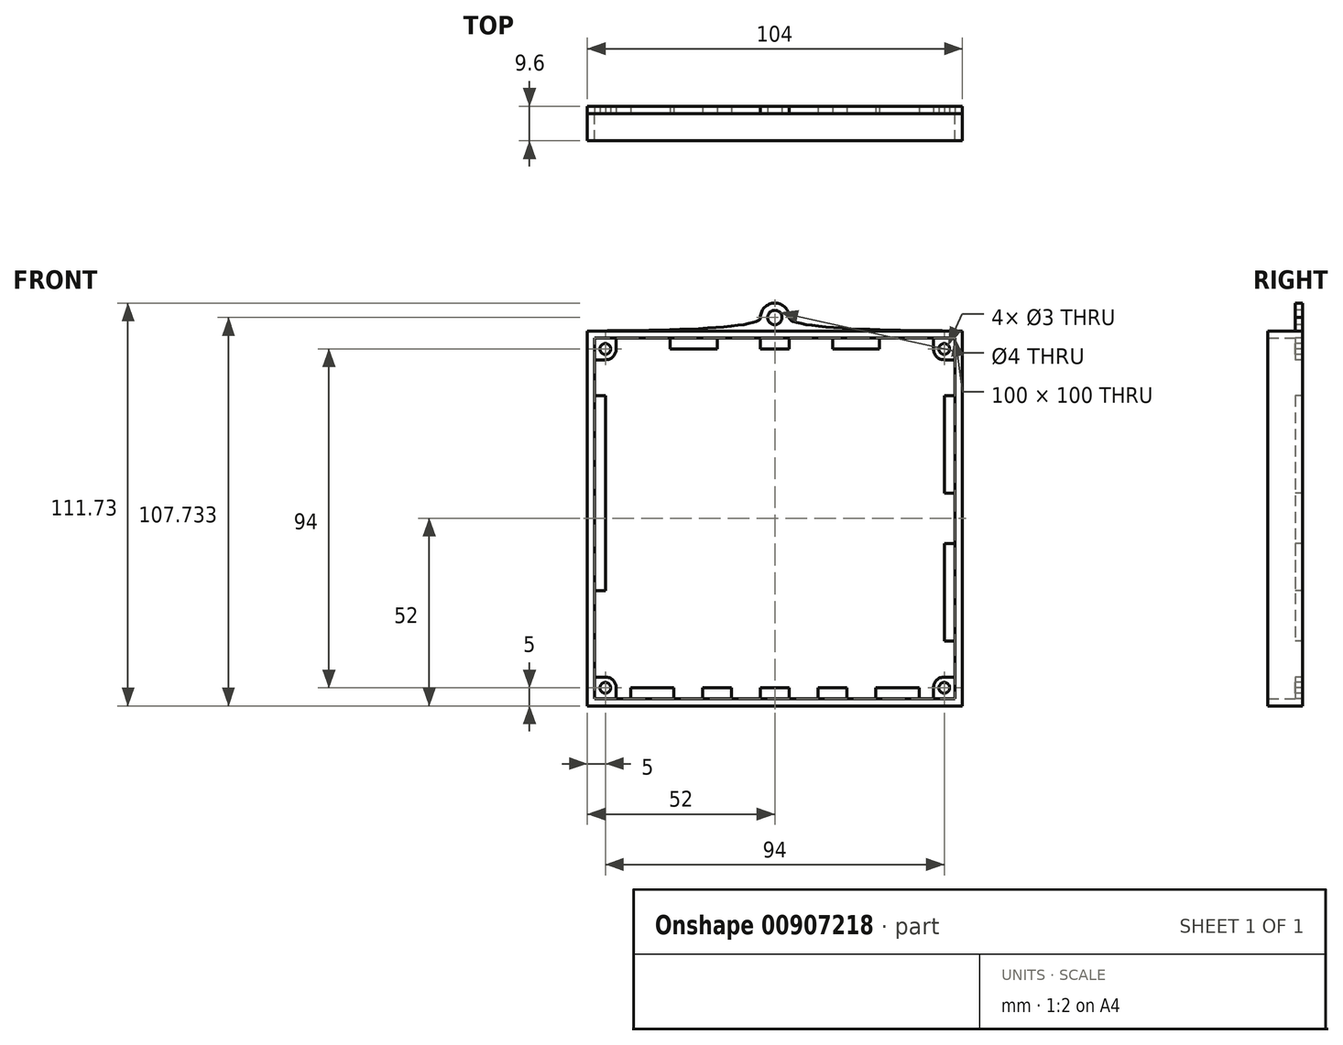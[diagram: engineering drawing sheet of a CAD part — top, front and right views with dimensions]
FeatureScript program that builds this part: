
annotation { "Feature Type Name" : "Feature", "Feature Type Description" : "" }
export const myFeature = defineFeature(function(context is Context, id is Id, definition is map)
    precondition{}
    {
        {
            var Q0;
            Q0=qCreatedBy(makeId("Front.planeOp"),FACE);
            var sketch = newSketch(context, id + "F0", { "sketchPlane" : qUnion([Q0])});
            skLineSegment(sketch, "E0.bottom", {"start": v(50, 50) * mm, "end": v(-50, 50) * mm});
            skLineSegment(sketch, "E0.top", {"start": v(50, -50) * mm, "end": v(-50, -50) * mm});
            skLineSegment(sketch, "E0.left", {"start": v(50, 50) * mm, "end": v(50, -50) * mm});
            skLineSegment(sketch, "E0.right", {"start": v(-50, 50) * mm, "end": v(-50, -50) * mm});
            skPoint(sketch, "E0.middle", {"position": v(0, 0) * mm});
            skLineSegment(sketch, "E1.bottom", {"start": v(-52, 52) * mm, "end": v(52, 52) * mm});
            skLineSegment(sketch, "E1.top", {"start": v(-52, -52) * mm, "end": v(52, -52) * mm});
            skLineSegment(sketch, "E1.left", {"start": v(-52, 52) * mm, "end": v(-52, -52) * mm});
            skLineSegment(sketch, "E1.right", {"start": v(52, 52) * mm, "end": v(52, -52) * mm});
            skSolve(sketch);
        }
        {
            var Q0;
            Q0 = qSketchRegion(id + "F0", true);
            extrude(context, id + "F1", {"entities" : qUnion([Q0]), "depth" : 7.6 * mm, "offsetDistance" : 25 * mm});
        }
        {
            var Q0;
            Q0=qCreatedBy(makeId("Front.planeOp"),FACE);
            var sketch = newSketch(context, id + "F2", { "sketchPlane" : qUnion([Q0])});
            skPoint(sketch, "E2.middle", {"position": v(0, 0) * mm});
            skCircle(sketch, "E3", {"center": v(47, 47) * mm, "radius": 1.5 * mm});
            skLineSegment(sketch, "E4.bottom", {"start": v(47, 47) * mm, "end": v(-47, 47) * mm, "construction": true});
            skLineSegment(sketch, "E4.top", {"start": v(47, -47) * mm, "end": v(-47, -47) * mm, "construction": true});
            skLineSegment(sketch, "E4.left", {"start": v(47, 47) * mm, "end": v(47, -47) * mm, "construction": true});
            skLineSegment(sketch, "E4.right", {"start": v(-47, 47) * mm, "end": v(-47, -47) * mm, "construction": true});
            skLineSegment(sketch, "E5.0", {"start": v(52, 52) * mm, "end": v(52, -52) * mm});
            skLineSegment(sketch, "E6.0", {"start": v(-52, 52) * mm, "end": v(52, 52) * mm, "construction": true});
            skLineSegment(sketch, "E7.0", {"start": v(-52, 52) * mm, "end": v(-52, -52) * mm});
            skLineSegment(sketch, "E8.0", {"start": v(-52, -52) * mm, "end": v(52, -52) * mm});
            skLineSegment(sketch, "E9.0", {"start": v(50, 50) * mm, "end": v(50, -50) * mm, "construction": true});
            skLineSegment(sketch, "E10.0", {"start": v(50, 50) * mm, "end": v(-50, 50) * mm, "construction": true});
            skLineSegment(sketch, "E11.0", {"start": v(-50, 50) * mm, "end": v(-50, -50) * mm, "construction": true});
            skLineSegment(sketch, "E12.0", {"start": v(50, -50) * mm, "end": v(-50, -50) * mm, "construction": true});
            skArc(sketch, "E13", {"start": v(47, 44) * mm, "mid": v(44.88, 44.88) * mm, "end": v(44, 47) * mm});
            skLineSegment(sketch, "E14", {"start": v(47, 44) * mm, "end": v(50, 44) * mm});
            skLineSegment(sketch, "E15", {"start": v(44, 47) * mm, "end": v(44, 50) * mm});
            skArc(sketch, "E16.MirrorCS", {"start": v(-47, 44) * mm, "mid": v(-44.88, 44.88) * mm, "end": v(-44, 47) * mm});
            skCircle(sketch, "E17.MirrorC", {"center": v(-47, 47) * mm, "radius": 1.5 * mm});
            skLineSegment(sketch, "E18.MirrorCS", {"start": v(-44, 47) * mm, "end": v(-44, 50) * mm});
            skLineSegment(sketch, "E19.MirrorCS", {"start": v(-47, 44) * mm, "end": v(-50, 44) * mm});
            skLineSegment(sketch, "E20.MirrorCS", {"start": v(47, -44) * mm, "end": v(50, -44) * mm});
            skArc(sketch, "E21.MirrorCS", {"start": v(47, -44) * mm, "mid": v(44.88, -44.88) * mm, "end": v(44, -47) * mm});
            skLineSegment(sketch, "E22.MirrorCS", {"start": v(44, -47) * mm, "end": v(44, -50) * mm});
            skCircle(sketch, "E23.MirrorC", {"center": v(47, -47) * mm, "radius": 1.5 * mm});
            skArc(sketch, "E24.MirrorCS", {"start": v(-47, -44) * mm, "mid": v(-44.88, -44.88) * mm, "end": v(-44, -47) * mm});
            skLineSegment(sketch, "E25.MirrorCS", {"start": v(-47, -44) * mm, "end": v(-50, -44) * mm});
            skLineSegment(sketch, "E26.MirrorCS", {"start": v(-44, -47) * mm, "end": v(-44, -50) * mm});
            skCircle(sketch, "E27.MirrorC", {"center": v(-47, -47) * mm, "radius": 1.5 * mm});
            skLineSegment(sketch, "E28", {"start": v(50, 44) * mm, "end": v(50, 34) * mm});
            skLineSegment(sketch, "E29", {"start": v(50, 34) * mm, "end": v(47, 34) * mm});
            skLineSegment(sketch, "E30", {"start": v(47, 34) * mm, "end": v(47, 7) * mm});
            skLineSegment(sketch, "E31", {"start": v(47, 7) * mm, "end": v(50, 7) * mm});
            skLineSegment(sketch, "E32", {"start": v(50, 7) * mm, "end": v(50, -7) * mm});
            skLineSegment(sketch, "E33", {"start": v(47, -7) * mm, "end": v(50, -7) * mm});
            skLineSegment(sketch, "E34", {"start": v(47, -7) * mm, "end": v(47, -34) * mm});
            skLineSegment(sketch, "E35", {"start": v(47, -34) * mm, "end": v(50, -34) * mm});
            skLineSegment(sketch, "E36", {"start": v(50, -34) * mm, "end": v(50, -44) * mm});
            skLineSegment(sketch, "E37", {"start": v(-50, 44) * mm, "end": v(-50, 34) * mm});
            skLineSegment(sketch, "E38", {"start": v(-50, 34) * mm, "end": v(-47, 34) * mm});
            skLineSegment(sketch, "E39", {"start": v(-47, 34) * mm, "end": v(-47, -20) * mm});
            skLineSegment(sketch, "E40", {"start": v(-47, -20) * mm, "end": v(-50, -20) * mm});
            skLineSegment(sketch, "E41", {"start": v(-50, -20) * mm, "end": v(-50, -44) * mm});
            skLineSegment(sketch, "E42", {"start": v(44, -50) * mm, "end": v(40, -50) * mm});
            skLineSegment(sketch, "E43", {"start": v(40, -50) * mm, "end": v(40, -47) * mm});
            skLineSegment(sketch, "E44", {"start": v(40, -47) * mm, "end": v(28, -47) * mm});
            skLineSegment(sketch, "E45", {"start": v(28, -47) * mm, "end": v(28, -50) * mm});
            skLineSegment(sketch, "E46", {"start": v(28, -50) * mm, "end": v(20, -50) * mm});
            skLineSegment(sketch, "E47", {"start": v(20, -50) * mm, "end": v(20, -47) * mm});
            skLineSegment(sketch, "E48", {"start": v(20, -47) * mm, "end": v(12, -47) * mm});
            skLineSegment(sketch, "E49", {"start": v(12, -47) * mm, "end": v(12, -50) * mm});
            skLineSegment(sketch, "E50", {"start": v(12, -50) * mm, "end": v(4, -50) * mm});
            skLineSegment(sketch, "E51", {"start": v(4, -50) * mm, "end": v(4, -47) * mm});
            skLineSegment(sketch, "E52", {"start": v(4, -47) * mm, "end": v(-4, -47) * mm});
            skLineSegment(sketch, "E53", {"start": v(-4, -47) * mm, "end": v(-4, -50) * mm});
            skLineSegment(sketch, "E54", {"start": v(-4, -50) * mm, "end": v(-12, -50) * mm});
            skLineSegment(sketch, "E55", {"start": v(-12, -50) * mm, "end": v(-12, -47) * mm});
            skLineSegment(sketch, "E56", {"start": v(-12, -47) * mm, "end": v(-20, -47) * mm});
            skLineSegment(sketch, "E57", {"start": v(-20, -47) * mm, "end": v(-20, -50) * mm});
            skLineSegment(sketch, "E58", {"start": v(-20, -50) * mm, "end": v(-28, -50) * mm});
            skLineSegment(sketch, "E59", {"start": v(-28, -50) * mm, "end": v(-28, -47) * mm});
            skLineSegment(sketch, "E60", {"start": v(-28, -47) * mm, "end": v(-40, -47) * mm});
            skLineSegment(sketch, "E61", {"start": v(-40, -47) * mm, "end": v(-40, -50) * mm});
            skLineSegment(sketch, "E62", {"start": v(-40, -50) * mm, "end": v(-44, -50) * mm});
            skLineSegment(sketch, "E63", {"start": v(44, 50) * mm, "end": v(29, 50) * mm});
            skLineSegment(sketch, "E64", {"start": v(29, 50) * mm, "end": v(29, 47) * mm});
            skLineSegment(sketch, "E65", {"start": v(29, 47) * mm, "end": v(16, 47) * mm});
            skLineSegment(sketch, "E66", {"start": v(16, 47) * mm, "end": v(16, 50) * mm});
            skLineSegment(sketch, "E67", {"start": v(16, 50) * mm, "end": v(4, 50) * mm});
            skLineSegment(sketch, "E68", {"start": v(4, 50) * mm, "end": v(4, 47) * mm});
            skLineSegment(sketch, "E69", {"start": v(4, 47) * mm, "end": v(-4, 47) * mm});
            skLineSegment(sketch, "E70", {"start": v(-4, 47) * mm, "end": v(-4, 50) * mm});
            skLineSegment(sketch, "E71", {"start": v(-4, 50) * mm, "end": v(-16, 50) * mm});
            skLineSegment(sketch, "E72", {"start": v(-16, 50) * mm, "end": v(-16, 47) * mm});
            skLineSegment(sketch, "E73", {"start": v(-16, 47) * mm, "end": v(-29, 47) * mm});
            skLineSegment(sketch, "E74", {"start": v(-29, 47) * mm, "end": v(-29, 50) * mm});
            skLineSegment(sketch, "E75", {"start": v(-29, 50) * mm, "end": v(-44, 50) * mm});
            skCircle(sketch, "E76", {"center": v(0, 55.73) * mm, "radius": 2 * mm});
            skArc(sketch, "E77", {"start": v(4, 55.73) * mm, "mid": v(0, 59.73) * mm, "end": v(-4, 55.73) * mm});
            skFitSpline(sketch, "E78", {"points": [v(52, 52) * mm, v(4, 55.73) * mm], "startDerivative": vector(-63.02, 0) * mm, "endDerivative": vector(1.95, 9.2) * mm});
            skFitSpline(sketch, "E79.MirrorCS", {"points": [v(-52, 52) * mm, v(-4, 55.73) * mm], "startDerivative": vector(63.02, 0) * mm, "endDerivative": vector(-1.95, 9.2) * mm});
            skSolve(sketch);
        }
        {
            var Q0;
            Q0 = qSketchRegion(id + "F2", true);
            extrude(context, id + "F3", {"entities" : qUnion([Q0]), "operationType" : NewBodyOperationType.ADD, "oppositeDirection" : true, "depth" : 2 * mm, "offsetDistance" : 25 * mm});
        }
    });
